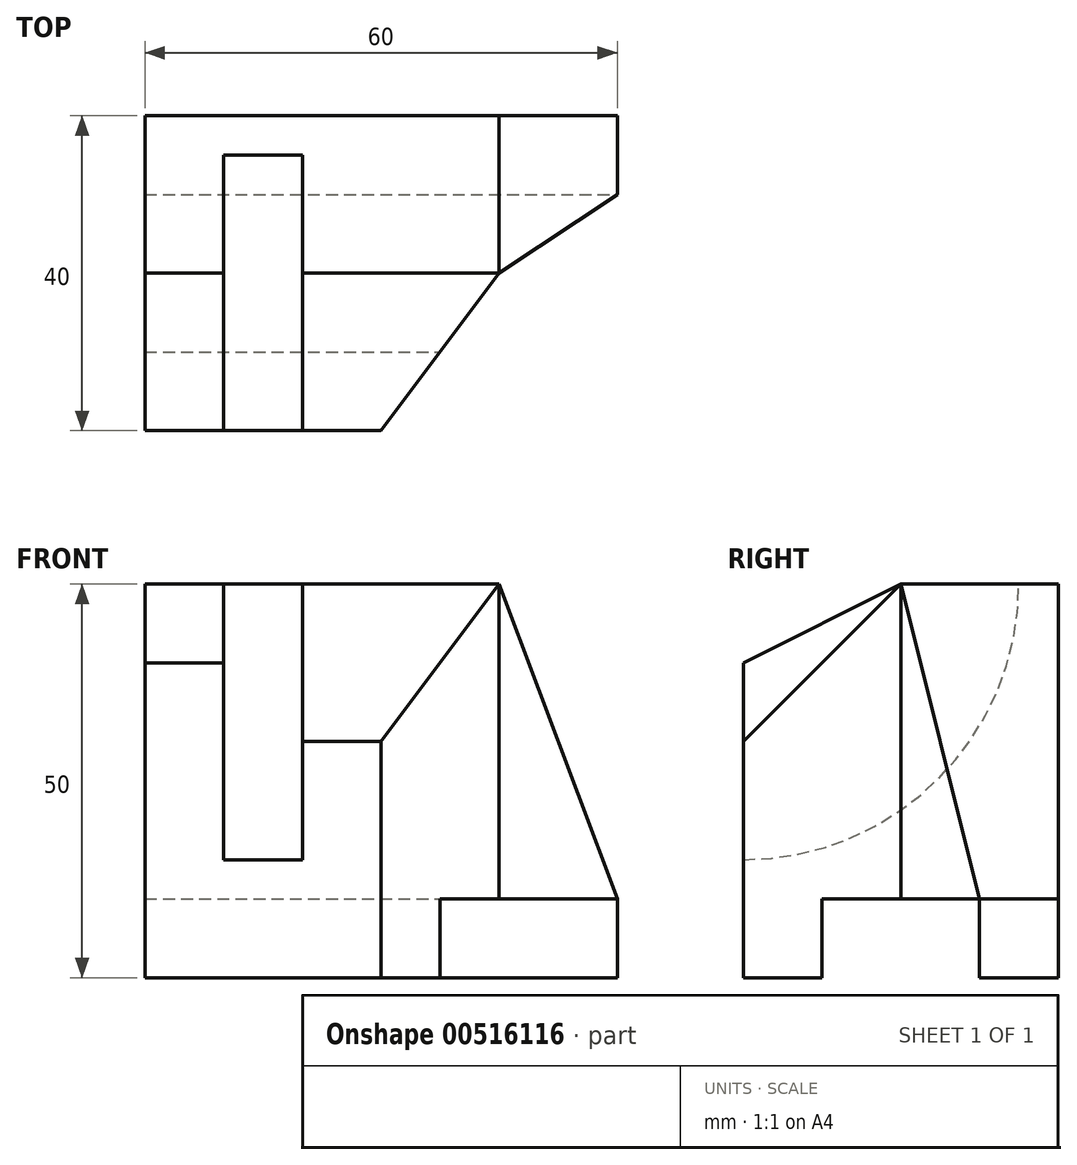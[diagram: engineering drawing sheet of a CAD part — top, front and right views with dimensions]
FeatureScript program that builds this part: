
annotation { "Feature Type Name" : "Feature", "Feature Type Description" : "" }
export const myFeature = defineFeature(function(context is Context, id is Id, definition is map)
    precondition{}
    {
        {
            var Q0;
            Q0=qCreatedBy(makeId("Top.planeOp"),FACE);
            var sketch = newSketch(context, id + "F0", { "sketchPlane" : qUnion([Q0])});
            skLineSegment(sketch, "E0.bottom", {"start": v(0, 0) * mm, "end": v(60, 0) * mm});
            skLineSegment(sketch, "E0.top", {"start": v(0, 40) * mm, "end": v(60, 40) * mm});
            skLineSegment(sketch, "E0.left", {"start": v(0, 0) * mm, "end": v(0, 40) * mm});
            skLineSegment(sketch, "E0.right", {"start": v(60, 0) * mm, "end": v(60, 40) * mm});
            skSolve(sketch);
        }
        {
            var Q0;
            Q0 = qSketchRegion(id + "F0", true);
            extrude(context, id + "F1", {"entities" : qUnion([Q0]), "depth" : 50 * mm, "offsetDistance" : 25 * mm});
        }
        {
            var Q0;
            Q0=makeQuery(id+"F1.opExtrude","CAP_FACE",FACE,{"disambiguationData":[OSD([sQuery(id+"F0.wireOp",EDGE,"E0.bottom"),sQuery(id+"F0.wireOp",EDGE,"E0.top"),sQuery(id+"F0.wireOp",EDGE,"E0.left"),sQuery(id+"F0.wireOp",EDGE,"E0.right")])],"isStart":true});
            var sketch = newSketch(context, id + "F2", { "sketchPlane" : qUnion([Q0])});
            skLineSegment(sketch, "E1.bottom", {"start": v(0, -10) * mm, "end": v(60, -10) * mm});
            skLineSegment(sketch, "E1.top", {"start": v(0, -30) * mm, "end": v(60, -30) * mm});
            skLineSegment(sketch, "E1.left", {"start": v(0, -10) * mm, "end": v(0, -30) * mm});
            skLineSegment(sketch, "E1.right", {"start": v(60, -10) * mm, "end": v(60, -30) * mm});
            skSolve(sketch);
        }
        {
            var Q0;
            Q0 = qSketchRegion(id + "F2", true);
            extrude(context, id + "F3", {"entities" : qUnion([Q0]), "operationType" : NewBodyOperationType.REMOVE, "oppositeDirection" : true, "depth" : 10 * mm, "offsetDistance" : 25 * mm});
        }
        {
            var Q0;
            Q0=makeQuery(id+"F1.opExtrude","CAP_FACE",FACE,{"disambiguationData":[OSD([sQuery(id+"F0.wireOp",EDGE,"E0.bottom"),sQuery(id+"F0.wireOp",EDGE,"E0.top"),sQuery(id+"F0.wireOp",EDGE,"E0.left"),sQuery(id+"F0.wireOp",EDGE,"E0.right")])],"isStart":false});
            var sketch = newSketch(context, id + "F4", { "sketchPlane" : qUnion([Q0])});
            skLineSegment(sketch, "E2.bottom", {"start": v(10, 0) * mm, "end": v(20, 0) * mm});
            skLineSegment(sketch, "E2.top", {"start": v(10, 35) * mm, "end": v(20, 35) * mm});
            skLineSegment(sketch, "E2.left", {"start": v(10, 0) * mm, "end": v(10, 35) * mm});
            skLineSegment(sketch, "E2.right", {"start": v(20, 0) * mm, "end": v(20, 35) * mm});
            skSolve(sketch);
        }
        {
            var Q0;
            Q0=makeQuery(id+"F1.opExtrude","SWEPT_FACE",FACE,{"disambiguationData":[OSD([sQuery(id+"F0.wireOp",EDGE,"E0.left")])]});
            var sketch = newSketch(context, id + "F5", { "sketchPlane" : qUnion([Q0])});
            skArc(sketch, "E3", {"start": v(0, 15) * mm, "mid": v(-24.75, 25.25) * mm, "end": v(-35, 50) * mm});
            skSolve(sketch);
        }
        {
            var Q0;
            Q0=makeQuery(id+"F4.imprint","IMPRINT",FACE,{"disambiguationData":[TD([[makeQuery(id+"F4.imprint","IMPRINT",EDGE,{"derivedFrom":sQuery(id+"F4.wireOp",EDGE,"E2.bottom")}),1.0]])]});
            var Q1;
            Q1=sQuery(id+"F5.wireOp",EDGE,"E3");
            sweep(context, id + "F6", {"operationType" : NewBodyOperationType.REMOVE, "profiles" : qUnion([Q0]), "path" : qUnion([Q1])});
        }
        {
            var Q0;
            Q0=makeQuery(id+"F1.opExtrude","CAP_FACE",FACE,{"disambiguationData":[OSD([sQuery(id+"F0.wireOp",EDGE,"E0.bottom"),sQuery(id+"F0.wireOp",EDGE,"E0.top"),sQuery(id+"F0.wireOp",EDGE,"E0.left"),sQuery(id+"F0.wireOp",EDGE,"E0.right")])],"isStart":false});
            var sketch = newSketch(context, id + "F7", { "sketchPlane" : qUnion([Q0])});
            skLineSegment(sketch, "E4.bottom", {"start": v(60, 40) * mm, "end": v(45, 40) * mm});
            skLineSegment(sketch, "E4.top", {"start": v(60, 0) * mm, "end": v(45, 0) * mm});
            skLineSegment(sketch, "E4.left", {"start": v(60, 40) * mm, "end": v(60, 0) * mm});
            skLineSegment(sketch, "E4.right", {"start": v(45, 40) * mm, "end": v(45, 0) * mm});
            skSolve(sketch);
        }
        {
            var Q0;
            Q0=sQuery(id+"F7.wireOp",VERTEX,"E4.right.start");
            var Q1;
            Q1=sQuery(id+"F7.wireOp",VERTEX,"E4.right.end");
            var Q2;
            Q2=makeQuery(id+"F3.boolean.opBoolean","COPY",VERTEX,{"derivedFrom":makeQuery(id+"F3.opExtrude","CAP_VERTEX",VERTEX,{"disambiguationData":[OSD([sQuery(id+"F0.wireOp",EDGE,"E0.right"),sQuery(id+"F2.wireOp",EDGE,"E1.top"),sQuery(id+"F2.wireOp",EDGE,"E1.right")])],"isStart":false})});
            cPlane(context, id + "F8", {"entities" : qUnion([Q0, Q1, Q2]), "cplaneType" : CPlaneType.THREE_POINT, "offset" : 25 * mm, "width" : 150 * mm, "height" : 150 * mm});
        }
        {
            var Q0;
            Q0=makeQuery(id+"F7.imprint","IMPRINT",FACE,{"disambiguationData":[TD([[makeQuery(id+"F7.imprint","IMPRINT",EDGE,{"derivedFrom":sQuery(id+"F7.wireOp",EDGE,"E4.bottom")}),-1.0]])]});
            var Q1;
            Q1=qCreatedBy(id+"F8.planeOp",FACE);
            extrude(context, id + "F9", {"entities" : qUnion([Q0]), "operationType" : NewBodyOperationType.REMOVE, "endBound" : BoundingType.UP_TO_SURFACE, "oppositeDirection" : true, "depth" : 25 * mm, "endBoundEntityFace" : qUnion([Q1]), "offsetDistance" : 25 * mm});
        }
        {
            var Q0;
            {var subQ0=sQuery(id+"F0.wireOp",EDGE,"E0.bottom");var subQ1=sQuery(id+"F0.wireOp",EDGE,"E0.right");Q0=makeQuery(id+"F6.boolean.opBoolean","SPLIT",EDGE,{"disambiguationData":[TD([makeQuery(id+"F1.opExtrude","SWEPT_FACE",FACE,{"disambiguationData":[OSD([subQ1])]})])],"derivedFrom":makeQuery(id+"F1.opExtrude","CAP_EDGE",EDGE,{"disambiguationData":[OSD([subQ0])],"isStart":false})});}
            chamfer(context, id + "F10", {"entities" : qUnion([Q0]), "chamferType" : ChamferType.TWO_OFFSETS, "width1" : 20 * mm, "oppositeDirection" : false, "width2" : 20 * mm, "tangentPropagation" : true});
        }
        {
            var Q0;
            {var subQ0=sQuery(id+"F0.wireOp",EDGE,"E0.bottom");var subQ1=sQuery(id+"F0.wireOp",EDGE,"E0.left");Q0=makeQuery(id+"F6.boolean.opBoolean","SPLIT",EDGE,{"disambiguationData":[TD([makeQuery(id+"F1.opExtrude","SWEPT_FACE",FACE,{"disambiguationData":[OSD([subQ1])]})])],"derivedFrom":makeQuery(id+"F1.opExtrude","CAP_EDGE",EDGE,{"disambiguationData":[OSD([subQ0])],"isStart":false})});}
            chamfer(context, id + "F11", {"entities" : qUnion([Q0]), "chamferType" : ChamferType.TWO_OFFSETS, "width1" : 20 * mm, "oppositeDirection" : false, "width2" : 10 * mm, "tangentPropagation" : true});
        }
        {
            var Q0;
            {var subQ0=sQuery(id+"F0.wireOp",EDGE,"E0.bottom");var subQ1=sQuery(id+"F0.wireOp",EDGE,"E0.right");var subQ2=sQuery(id+"F0.wireOp",EDGE,"E0.left");Q0=makeQuery(id+"F3.boolean.opBoolean","SPLIT",FACE,{"disambiguationData":[TD([makeQuery(id+"F1.opExtrude","SWEPT_FACE",FACE,{"disambiguationData":[OSD([subQ0])]})])],"derivedFrom":makeQuery(id+"F1.opExtrude","CAP_FACE",FACE,{"disambiguationData":[OSD([subQ0,sQuery(id+"F0.wireOp",EDGE,"E0.top"),subQ2,subQ1])],"isStart":true})});}
            var sketch = newSketch(context, id + "F12", { "sketchPlane" : qUnion([Q0])});
            skLineSegment(sketch, "E5", {"start": v(30, 0) * mm, "end": v(45, -20) * mm});
            skLineSegment(sketch, "E6", {"start": v(45, -20) * mm, "end": v(60, -30) * mm});
            skLineSegment(sketch, "E7", {"start": v(60, -30) * mm, "end": v(60, 0) * mm});
            skLineSegment(sketch, "E8", {"start": v(60, 0) * mm, "end": v(30, 0) * mm});
            skSolve(sketch);
        }
        {
            var Q0;
            {var subQ0=sQuery(id+"F12.wireOp",EDGE,"E6");Q0=makeQuery(id+"F12.imprint","IMPRINT",FACE,{"disambiguationData":[TD([[makeQuery(id+"F12.imprint","IMPRINT",EDGE,{"derivedFrom":subQ0}),1.0]])]});}
            var Q1;
            {var subQ0=sQuery(id+"F12.wireOp",EDGE,"E8");Q1=makeQuery(id+"F12.imprint","IMPRINT",FACE,{"disambiguationData":[TD([[makeQuery(id+"F12.imprint","IMPRINT",EDGE,{"derivedFrom":subQ0}),-1.0]])]});}
            var Q2;
            {var subQ0=sQuery(id+"F0.wireOp",EDGE,"E0.right");var subQ1=sQuery(id+"F0.wireOp",EDGE,"E0.bottom");var subQ2=makeQuery(id+"F1.opExtrude","CAP_FACE",FACE,{"disambiguationData":[OSD([subQ1,sQuery(id+"F0.wireOp",EDGE,"E0.top"),sQuery(id+"F0.wireOp",EDGE,"E0.left"),subQ0])],"isStart":false});Q2=makeQuery(id+"F10.opChamfer","BLEND_VERTEX",VERTEX,{"blendedFrom":[makeQuery(id+"F6.boolean.opBoolean","SPLIT",EDGE,{"disambiguationData":[TD([makeQuery(id+"F1.opExtrude","SWEPT_FACE",FACE,{"disambiguationData":[OSD([subQ0])]})])],"derivedFrom":makeQuery(id+"F1.opExtrude","CAP_EDGE",EDGE,{"disambiguationData":[OSD([subQ1])],"isStart":false})}),makeQuery(id+"F9.boolean.opBoolean","COPY",FACE,{"derivedFrom":makeQuery(id+"F9.opExtrude","CAP_FACE",FACE,{"disambiguationData":[OSD([sQuery(id+"F7.wireOp",EDGE,"E4.bottom"),sQuery(id+"F7.wireOp",EDGE,"E4.top"),sQuery(id+"F7.wireOp",EDGE,"E4.left"),sQuery(id+"F7.wireOp",EDGE,"E4.right")])],"isStart":false})}),subQ2],"blendedInto":[makeQuery(id+"F9.boolean.opBoolean","COPY",FACE,{"derivedFrom":makeQuery(id+"F9.opExtrude","CAP_FACE",FACE,{"disambiguationData":[OSD([sQuery(id+"F7.wireOp",EDGE,"E4.bottom"),sQuery(id+"F7.wireOp",EDGE,"E4.top"),sQuery(id+"F7.wireOp",EDGE,"E4.left"),sQuery(id+"F7.wireOp",EDGE,"E4.right")])],"isStart":false})}),subQ2]});}
            extrude(context, id + "F13", {"entities" : qUnion([Q0, Q1]), "operationType" : NewBodyOperationType.REMOVE, "endBound" : BoundingType.UP_TO_VERTEX, "oppositeDirection" : true, "depth" : 25 * mm, "endBoundEntityVertex" : qUnion([Q2]), "offsetDistance" : 25 * mm});
        }
    });
